# Revit family: 1408006 - Fold Table LED-
name_source: partatom
category: Lighting Fixtures
revit_build: Autodesk Revit 2018 (Build: 20170223_1515(x64)
units: mm (PartAtom-declared; Revit-internal decimal feet)

## family parameters
Always vertical = Yes
Cut with Voids When Loaded = No
Light Source = Yes
OmniClass Number = 23.80.70.00
OmniClass Title = Lighting
Part Type = Normal
Room Calculation Point = No
Round Connector Dimension = Use Diameter
Shared = No
Work Plane-Based = No

## types (1)
- CE
    Apparent Load = 11 VA
    Color Filter = 16777215
    Dimmable = Non-Dimming
    Dimming Lamp Color Temperature Shift = <None>
    Driver Included = Yes
    Driver Required = No
    Efficacy (lm/W) = 30
    Electrical Class = 2
    Emit from Line Length = 25 mm  [stored 0.082021 ft]
    Lamp = Citizen CL-L104
    Light Source Fixed = Adjustable
    Light Source Symbol Length = 416 mm
    Location Rating = Zone 3
    Main Finish = Matt Nickel
    Main Material = Metal - Aluminium
    Power (W) = 3
    Prdouct Code = -
    Product Location = Indoor
    Product Name = Fold Table LED
    Product SKU = 1408006
    Spot Beam Angle = 60.00°
    Spot Field Angle = 60.00°
    Tilt Angle = 90.00°

note: [stored X ft] marks values corroborated as IEEE doubles in the binary element streams (Revit-internal decimal feet)

## geometry (parser evidence)
native form markers: Sweep x2
no freeform markers — native parametric forms only
